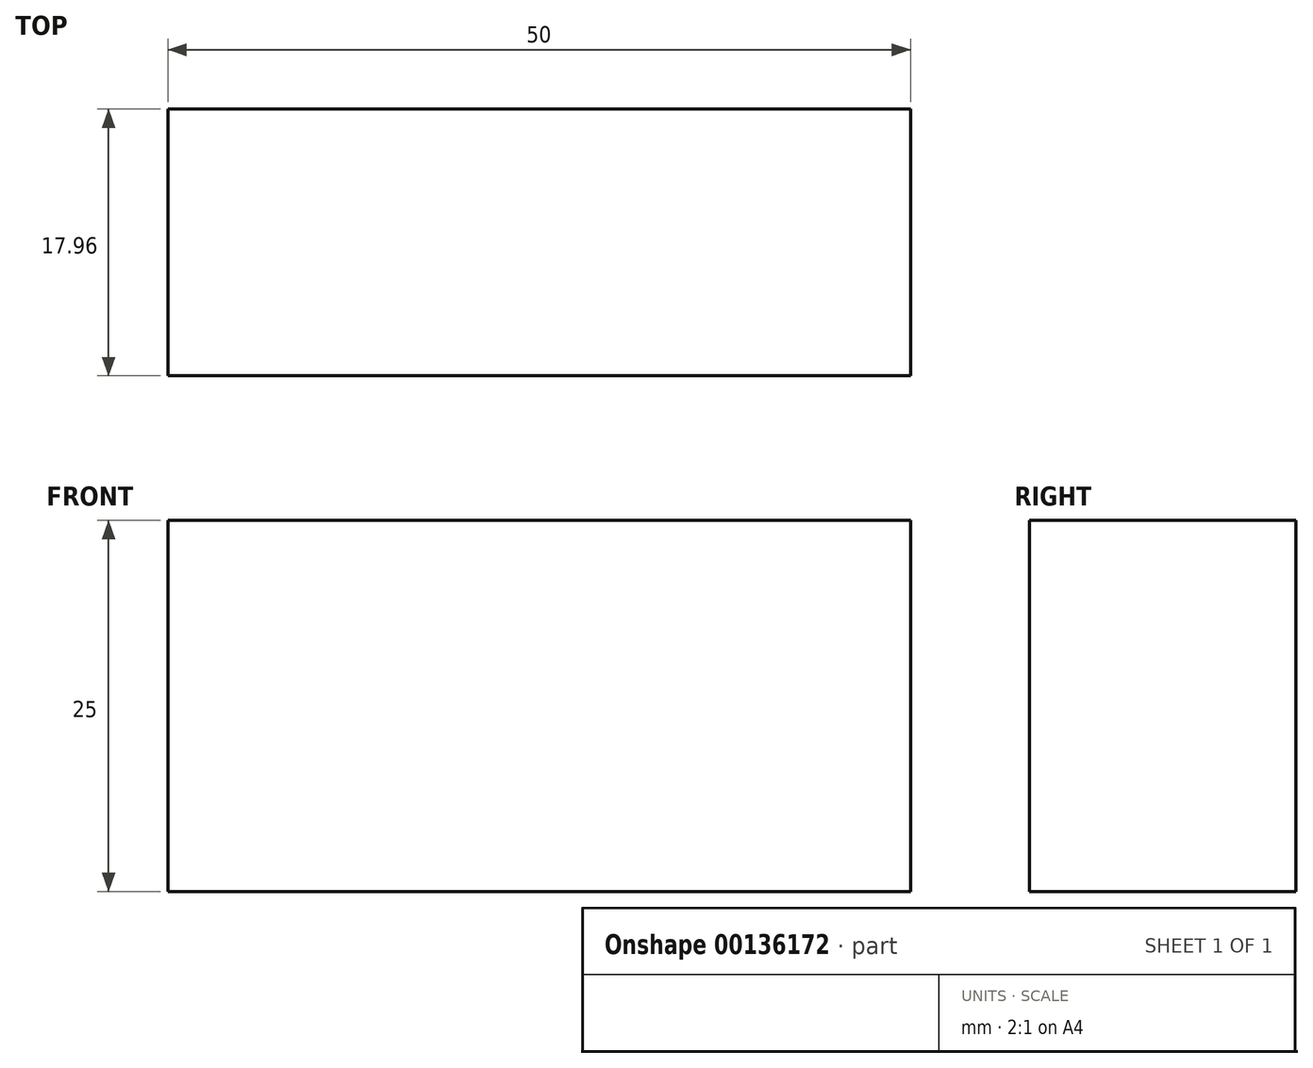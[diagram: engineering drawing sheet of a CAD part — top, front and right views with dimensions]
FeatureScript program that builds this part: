
annotation { "Feature Type Name" : "Feature", "Feature Type Description" : "" }
export const myFeature = defineFeature(function(context is Context, id is Id, definition is map)
    precondition{}
    {
        {
            var Q0;
            Q0=qCreatedBy(makeId("Top.planeOp"),FACE);
            var sketch = newSketch(context, id + "F0", { "sketchPlane" : qUnion([Q0])});
            skLineSegment(sketch, "E0.bottom", {"start": v(-50, -8.98) * mm, "end": v(0, -8.98) * mm});
            skLineSegment(sketch, "E0.top", {"start": v(-50, 8.98) * mm, "end": v(0, 8.98) * mm});
            skLineSegment(sketch, "E0.left", {"start": v(-50, -8.98) * mm, "end": v(-50, 8.98) * mm});
            skLineSegment(sketch, "E0.right", {"start": v(0, -8.98) * mm, "end": v(0, 8.98) * mm});
            skSolve(sketch);
        }
        {
            var Q0;
            Q0=makeQuery(id+"F0.imprint","IMPRINT",FACE,{"disambiguationData":[TD([[makeQuery(id+"F0.imprint","IMPRINT",EDGE,{"derivedFrom":sQuery(id+"F0.wireOp",EDGE,"E0.bottom")}),1.0]])]});
            extrude(context, id + "F1", {"entities" : qUnion([Q0]), "endBound" : BoundingType.SYMMETRIC, "depth" : 25 * mm});
        }
    });
